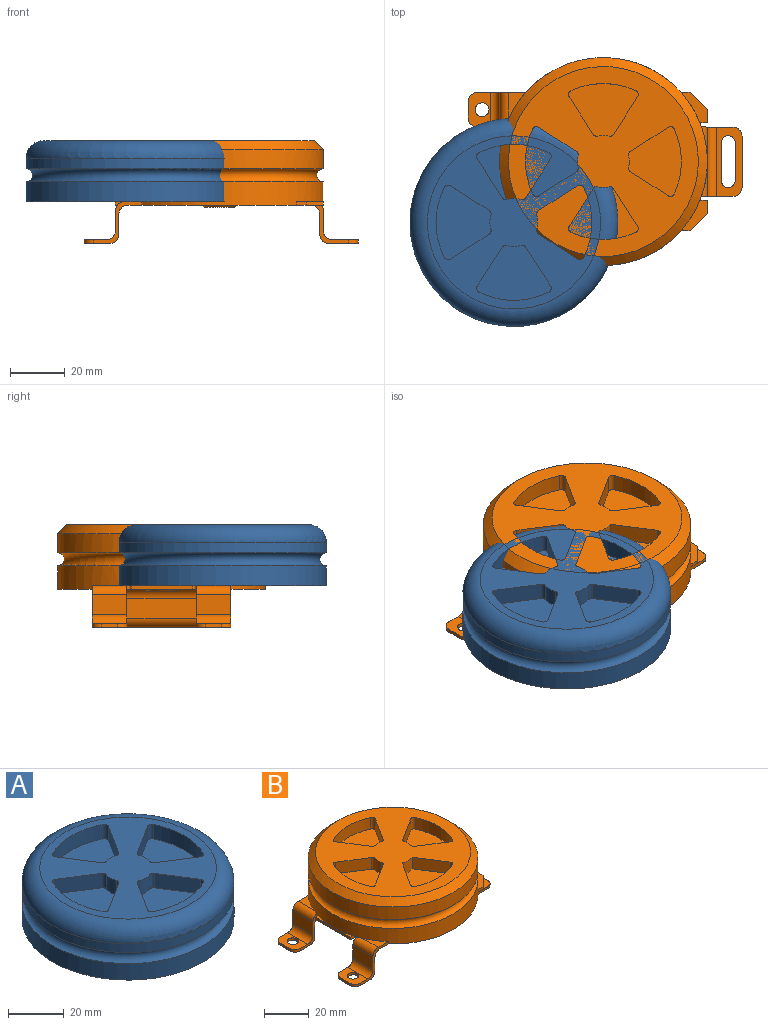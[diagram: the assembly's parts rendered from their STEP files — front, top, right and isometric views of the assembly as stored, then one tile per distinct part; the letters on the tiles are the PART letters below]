
ASSEMBLY  parts=2 mates=1
PART A: 48 faces, bbox 86.2x86.2x22.4 mm
  f0: cylinder r=38.1mm len=76.2mm, axis (0,0,-1), area 942.5mm2, adj f38,f41
  f1: plane 63.5x63.5mm, normal (0,0,1), area 1688.4mm2, adj f2,f3,f4,f5,f7,f8,f9,f10
  f2: cylinder r=28.57mm len=25.69mm, axis (0,0,1), area 169.2mm2, adj f1,f6,f34,f37
  f3: plane 14.28x9.1mm, normal (0.54,-0.84,0), area 107.5mm2, adj f1,f6,f36,f37
  f4: cylinder r=8.82mm len=6.35mm, axis (0,0,1), area 33.7mm2, adj f1,f6,f35,f36
  f5: plane 14.28x9.1mm, normal (0.54,0.84,0), area 107.5mm2, adj f1,f6,f34,f35
  f6: plane 27.37x20.21mm, normal (0,0,1), area 369.6mm2, adj f2,f3,f4,f5,f34,f35,f36,f37
  f7: cylinder r=8.82mm len=6.35mm, axis (0,0,1), area 33.7mm2, adj f1,f11,f22,f25
  f8: plane 14.28x9.1mm, normal (0.84,-0.54,0), area 107.5mm2, adj f1,f11,f24,f25
  f9: cylinder r=28.57mm len=25.69mm, axis (0,0,1), area 169.2mm2, adj f1,f11,f23,f24
  f10: plane 14.28x9.1mm, normal (-0.84,-0.54,0), area 107.5mm2, adj f1,f11,f22,f23
  f11: plane 27.37x20.21mm, normal (0,0,1), area 369.6mm2, adj f7,f8,f9,f10,f22,f23,f24,f25
  f12: cylinder r=8.82mm len=6.35mm, axis (0,0,1), area 33.7mm2, adj f1,f16,f30,f33
  f13: plane 14.28x9.1mm, normal (-0.84,0.54,0), area 107.5mm2, adj f1,f16,f30,f31
  f14: cylinder r=28.57mm len=25.69mm, axis (0,0,1), area 169.2mm2, adj f1,f16,f31,f32
  f15: plane 14.28x9.1mm, normal (0.84,0.54,0), area 107.5mm2, adj f1,f16,f32,f33
  f16: plane 27.37x20.21mm, normal (0,0,1), area 369.6mm2, adj f12,f13,f14,f15,f30,f31,f32,f33
  f17: cylinder r=8.82mm len=6.35mm, axis (0,0,1), area 33.7mm2, adj f1,f21,f26,f29
  f18: plane 14.28x9.1mm, normal (-0.54,-0.84,0), area 107.5mm2, adj f1,f21,f28,f29
  f19: cylinder r=28.57mm len=25.69mm, axis (0,0,1), area 169.2mm2, adj f1,f21,f27,f28
  f20: plane 14.28x9.1mm, normal (-0.54,0.84,0), area 107.5mm2, adj f1,f21,f26,f27
  f21: plane 27.37x20.21mm, normal (0,0,1), area 369.6mm2, adj f17,f18,f19,f20,f26,f27,f28,f29
  f22: cylinder r=1.52mm len=6.35mm, axis (0,0,1), area 12.6mm2, adj f1,f7,f10,f11
  f23: cylinder r=1.52mm len=6.35mm, axis (0,0,1), area 16.2mm2, adj f1,f9,f10,f11
  f24: cylinder r=1.52mm len=6.35mm, axis (0,0,1), area 16.2mm2, adj f1,f8,f9,f11
  f25: cylinder r=1.52mm len=6.35mm, axis (0,0,1), area 12.6mm2, adj f1,f7,f8,f11
  f26: cylinder r=1.52mm len=6.35mm, axis (0,0,1), area 12.6mm2, adj f1,f17,f20,f21
  f27: cylinder r=1.52mm len=6.35mm, axis (0,0,1), area 16.2mm2, adj f1,f19,f20,f21
  f28: cylinder r=1.52mm len=6.35mm, axis (0,0,1), area 16.2mm2, adj f1,f18,f19,f21
  f29: cylinder r=1.52mm len=6.35mm, axis (0,0,1), area 12.6mm2, adj f1,f17,f18,f21
  f30: cylinder r=1.52mm len=6.35mm, axis (0,0,1), area 12.6mm2, adj f1,f12,f13,f16
  f31: cylinder r=1.52mm len=6.35mm, axis (0,0,1), area 16.2mm2, adj f1,f13,f14,f16
  f32: cylinder r=1.52mm len=6.35mm, axis (0,0,1), area 16.2mm2, adj f1,f14,f15,f16
  f33: cylinder r=1.52mm len=6.35mm, axis (0,0,1), area 12.6mm2, adj f1,f12,f15,f16
  f34: cylinder r=1.52mm len=6.35mm, axis (0,0,1), area 16.2mm2, adj f1,f2,f5,f6
  f35: cylinder r=1.52mm len=6.35mm, axis (0,0,1), area 12.6mm2, adj f1,f4,f5,f6
  f36: cylinder r=1.52mm len=6.35mm, axis (0,0,1), area 12.6mm2, adj f1,f3,f4,f6
  f37: cylinder r=1.52mm len=6.35mm, axis (0,0,1), area 16.2mm2, adj f1,f2,f3,f6
  f38: torus R=38.1mm, axis (0,0,1), area 1741.6mm2, adj f0,f40
  f39: plane 76.2x76.2mm, normal (0,0,-1), area 4465.4mm2, adj f40,f42,f44,f46
  f40: cylinder r=38.1mm len=76.2mm, axis (0,0,-1), area 1732.9mm2, adj f38,f39
  f41: torus R=31.75mm, axis (0,0,1), area 2243.2mm2, adj f0,f1
  f42: cylinder r=3.17mm len=15.24mm, axis (0,0,-1), area 304mm2, adj f39,f43
  f43: plane 6.35x6.35mm, normal (0,0,-1), area 31.7mm2, adj f42
  f44: cylinder r=3.17mm len=15.24mm, axis (0,0,-1), area 304mm2, adj f39,f45
  f45: plane 6.35x6.35mm, normal (0,0,-1), area 31.7mm2, adj f44
  f46: cylinder r=3.17mm len=15.24mm, axis (0,0,-1), area 304mm2, adj f39,f47
  f47: plane 6.35x6.35mm, normal (0,0,-1), area 31.7mm2, adj f46
PART B: 111 faces, bbox 100.3x86.2x37.6 mm
  f0: plane 69.6x69.6mm, normal (0,0,1), area 2498.2mm2, adj f74,f75,f76,f77,f79,f80,f81,f82
  f1: cylinder r=38.1mm len=76.2mm, axis (0,0,-1), area 1895.7mm2, adj f2,f3,f4,f5,f6,f9,f10,f13
  f2: plane 11.18x9.7mm, normal (0,0,1), area 44.4mm2, adj f1,f17,f18,f47,f53
  f3: plane 9.89x6.4mm, normal (0,0,1), area 28mm2, adj f1,f16,f27
  f4: plane 11.18x1.68mm, normal (0,0,1), area 6.2mm2, adj f1,f11,f24
  f5: plane 11.18x1.68mm, normal (0,0,1), area 6.2mm2, adj f1,f11,f23
  f6: plane 9.89x6.4mm, normal (0,0,1), area 28mm2, adj f1,f14,f28
  f7: plane 25.4x7.37mm, normal (1,0,0), area 187.1mm2, adj f49,f50,f66,f68
  f8: plane 4.83x1.27mm, normal (1,0,0), area 6.1mm2, adj f9,f10,f48,f52
  f9: plane 11.18x9.7mm, normal (0,0,1), area 44.4mm2, adj f1,f8,f13,f48,f52
  f10: plane 76.2x76.2mm, normal (0,0,-1), area 4443.5mm2, adj f1,f8,f11,f13,f14,f16,f17,f18
  f11: plane 22.35x1.27mm, normal (-1,0,0), area 28.4mm2, adj f4,f5,f10,f23,f24
  f12: plane 12.7x7.37mm, normal (-1,0,0), area 93.5mm2, adj f14,f21,f28,f45
  f13: plane 3.35x1.27mm, normal (0,1,0), area 4.3mm2, adj f1,f9,f10,f48
  f14: plane 17.83x15.24mm, normal (0,1,0), area 40.4mm2, adj f1,f6,f10,f12,f22,f28,f29,f37
  f15: plane 12.7x7.37mm, normal (-1,0,0), area 93.5mm2, adj f16,f20,f27,f46
  f16: plane 17.83x15.24mm, normal (0,-1,0), area 40.4mm2, adj f1,f3,f10,f15,f19,f27,f30,f33
  f17: plane 3.35x1.27mm, normal (0,-1,0), area 4.3mm2, adj f1,f2,f10,f47
  f18: plane 4.83x1.27mm, normal (1,0,0), area 6.1mm2, adj f2,f10,f47,f53
  f19: plane 12.7x7.37mm, normal (1,0,0), area 93.5mm2, adj f16,f20,f30,f44
  f20: plane 15.24x11.94mm, normal (0,1,0), area 32.9mm2, adj f15,f19,f26,f27,f30,f33,f34,f43
  f21: plane 15.24x11.94mm, normal (0,-1,0), area 32.9mm2, adj f12,f22,f25,f28,f29,f37,f38,f40
  f22: plane 12.7x7.37mm, normal (1,0,0), area 93.5mm2, adj f14,f21,f29,f41
  f23: plane 3.81x1.27mm, normal (0,1,0), area 4.8mm2, adj f5,f10,f11,f25,f70
  f24: plane 3.81x1.27mm, normal (0,-1,0), area 4.8mm2, adj f4,f10,f11,f26,f71
  f25: cylinder r=0.76mm len=1.52mm, axis (0,0,-1), area 3.1mm2, adj f10,f21,f23,f29,f70
  f26: cylinder r=0.76mm len=1.52mm, axis (0,0,-1), area 3.1mm2, adj f10,f20,f24,f30,f71
  f27: cylinder r=3.3mm len=12.7mm, axis (0,1,0), area 65.9mm2, adj f3,f15,f16,f20,f71
  f28: cylinder r=3.3mm len=12.7mm, axis (0,1,0), area 65.9mm2, adj f6,f12,f14,f21,f70
  f29: cylinder r=3.3mm len=13.46mm, axis (0,1,0), area 66mm2, adj f10,f14,f21,f22,f25
  f30: cylinder r=3.3mm len=13.46mm, axis (0,1,0), area 66mm2, adj f10,f16,f19,f20,f26
  f31: plane 6.1x1.27mm, normal (-1,0,0), area 7.7mm2, adj f33,f34,f42,f43
  f32: cylinder r=2.54mm len=5.08mm, axis (0,0,1), area 20.3mm2, adj f33,f34
  f33: plane 12.7x9.4mm, normal (0,0,-1), area 94.4mm2, adj f16,f20,f31,f32,f42,f43,f44
  f34: plane 12.7x8.13mm, normal (0,0,1), area 78.3mm2, adj f16,f20,f31,f32,f42,f43,f46
  f35: plane 6.1x1.27mm, normal (-1,0,0), area 7.7mm2, adj f37,f38,f39,f40
  f36: cylinder r=2.54mm len=5.08mm, axis (0,0,1), area 20.3mm2, adj f37,f38
  f37: plane 12.7x9.4mm, normal (0,0,-1), area 94.4mm2, adj f14,f21,f35,f36,f39,f40,f41
  f38: plane 12.7x8.13mm, normal (0,0,1), area 78.3mm2, adj f14,f21,f35,f36,f39,f40,f45
  f39: cylinder r=3.3mm len=3.3mm, axis (0,0,-1), area 6.6mm2, adj f14,f35,f37,f38
  f40: cylinder r=3.3mm len=3.3mm, axis (0,0,1), area 6.6mm2, adj f21,f35,f37,f38
  f41: cylinder r=3.3mm len=12.7mm, axis (0,1,0), area 65.9mm2, adj f14,f21,f22,f37
  f42: cylinder r=3.3mm len=3.3mm, axis (0,0,1), area 6.6mm2, adj f16,f31,f33,f34
  f43: cylinder r=3.3mm len=3.3mm, axis (0,0,1), area 6.6mm2, adj f20,f31,f33,f34
  f44: cylinder r=3.3mm len=12.7mm, axis (0,1,0), area 65.9mm2, adj f16,f19,f20,f33
  f45: cylinder r=3.3mm len=12.7mm, axis (0,1,0), area 65.9mm2, adj f12,f14,f21,f38
  f46: cylinder r=3.3mm len=12.7mm, axis (0,1,0), area 65.9mm2, adj f15,f16,f20,f34
  f47: plane 6.35x6.35mm, normal (0.71,-0.71,0), area 11.4mm2, adj f2,f10,f17,f18
  f48: plane 6.35x6.35mm, normal (0.71,0.71,0), area 11.4mm2, adj f8,f9,f10,f13
  f49: plane 15.24x13.21mm, normal (0,1,0), area 34.5mm2, adj f7,f51,f54,f56,f62,f63,f65,f66
  f50: plane 15.24x13.21mm, normal (0,-1,0), area 34.5mm2, adj f7,f51,f55,f56,f62,f64,f65,f66
  f51: plane 25.4x7.37mm, normal (-1,0,0), area 187.1mm2, adj f49,f50,f65,f67
  f52: plane 3.81x1.27mm, normal (0,-1,0), area 4.8mm2, adj f8,f9,f10,f54,f69
  f53: plane 3.81x1.27mm, normal (0,1,0), area 4.8mm2, adj f2,f10,f18,f55,f69
  f54: cylinder r=0.76mm len=1.52mm, axis (0,0,-1), area 3.1mm2, adj f10,f49,f52,f67,f69
  f55: cylinder r=0.76mm len=1.52mm, axis (0,0,-1), area 3.1mm2, adj f10,f50,f53,f67,f69
  f56: plane 25.4x9.4mm, normal (0,0,1), area 142.8mm2, adj f49,f50,f57,f58,f59,f60,f61,f63
  f57: plane 13.97x1.27mm, normal (-1,0,0), area 17.7mm2, adj f56,f58,f61,f62
  f58: cylinder r=2.54mm len=5.08mm, axis (0,0,1), area 10.1mm2, adj f56,f57,f59,f62
  f59: plane 13.97x1.27mm, normal (1,0,0), area 17.7mm2, adj f56,f58,f61,f62
  f60: plane 18.8x1.27mm, normal (1,0,0), area 23.9mm2, adj f56,f62,f63,f64
  f61: cylinder r=2.54mm len=5.08mm, axis (0,0,1), area 10.1mm2, adj f56,f57,f59,f62
  f62: plane 25.4x10.67mm, normal (0,0,-1), area 175.1mm2, adj f49,f50,f57,f58,f59,f60,f61,f63
  f63: cylinder r=3.3mm len=3.3mm, axis (0,0,1), area 6.6mm2, adj f49,f56,f60,f62
  f64: cylinder r=3.3mm len=3.3mm, axis (0,0,-1), area 6.6mm2, adj f50,f56,f60,f62
  f65: cylinder r=3.3mm len=25.4mm, axis (0,-1,0), area 131.7mm2, adj f49,f50,f51,f62
  f66: cylinder r=3.3mm len=25.4mm, axis (0,-1,0), area 131.7mm2, adj f7,f49,f50,f69
  f67: cylinder r=3.3mm len=26.92mm, axis (0,-1,0), area 132mm2, adj f10,f49,f50,f51,f54,f55
  f68: cylinder r=3.3mm len=25.4mm, axis (0,-1,0), area 131.7mm2, adj f7,f49,f50,f56
  f69: plane 28.45x4.57mm, normal (0,0,-1), area 71.6mm2, adj f1,f49,f50,f52,f53,f54,f55,f66
  f70: plane 4.34x2.9mm, normal (0,0,-1), area 5.4mm2, adj f1,f21,f23,f25,f28
  f71: plane 4.34x2.9mm, normal (0,0,-1), area 5.4mm2, adj f1,f20,f24,f26,f27
  f72: torus R=38.1mm, axis (0,0,1), area 1741.6mm2, adj f1,f73
  f73: cylinder r=38.1mm len=76.2mm, axis (0,0,-1), area 1672.1mm2, adj f72,f108
  f74: cylinder r=9.53mm len=6.35mm, axis (0,0,1), area 40.6mm2, adj f0,f75,f77,f78
  f75: plane 14.78x9.42mm, normal (0.84,-0.54,0), area 111.3mm2, adj f0,f74,f78,f107
  f76: cylinder r=28.57mm len=23.81mm, axis (0,0,1), area 155.9mm2, adj f0,f78,f106,f107
  f77: plane 14.78x9.42mm, normal (-0.84,-0.54,0), area 111.3mm2, adj f0,f74,f78,f106
  f78: plane 25.58x19.58mm, normal (0,0,1), area 326.8mm2, adj f74,f75,f76,f77,f106,f107
  f79: cylinder r=9.53mm len=6.35mm, axis (0,0,1), area 27.2mm2, adj f0,f83,f95,f96
  f80: plane 13.82x8.81mm, normal (-0.54,-0.84,0), area 104.1mm2, adj f0,f83,f94,f95
  f81: cylinder r=28.57mm len=23.81mm, axis (0,0,1), area 155.9mm2, adj f0,f83,f94,f97
  f82: plane 13.82x8.81mm, normal (-0.54,0.84,0), area 104.1mm2, adj f0,f83,f96,f97
  f83: plane 25.58x19.33mm, normal (0,0,1), area 326.4mm2, adj f79,f80,f81,f82,f94,f95,f96,f97
  f84: cylinder r=9.53mm len=6.35mm, axis (0,0,1), area 27.2mm2, adj f0,f88,f102,f105
  f85: plane 13.82x8.81mm, normal (0.54,0.84,0), area 104.1mm2, adj f0,f88,f102,f103
  f86: cylinder r=28.57mm len=23.81mm, axis (0,0,1), area 155.9mm2, adj f0,f88,f103,f104
  f87: plane 13.82x8.81mm, normal (0.54,-0.84,0), area 104.1mm2, adj f0,f88,f104,f105
  f88: plane 25.58x19.33mm, normal (0,0,1), area 326.4mm2, adj f84,f85,f86,f87,f102,f103,f104,f105
  f89: cylinder r=9.53mm len=6.35mm, axis (0,0,1), area 27.2mm2, adj f0,f93,f98,f101
  f90: plane 13.82x8.81mm, normal (-0.84,0.54,0), area 104.1mm2, adj f0,f93,f100,f101
  f91: cylinder r=28.57mm len=23.81mm, axis (0,0,1), area 155.9mm2, adj f0,f93,f99,f100
  f92: plane 13.82x8.81mm, normal (0.84,0.54,0), area 104.1mm2, adj f0,f93,f98,f99
  f93: plane 25.58x19.33mm, normal (0,0,1), area 326.4mm2, adj f89,f90,f91,f92,f98,f99,f100,f101
  f94: cylinder r=1.52mm len=6.35mm, axis (0,0,1), area 16.5mm2, adj f0,f80,f81,f83
  f95: cylinder r=1.52mm len=6.35mm, axis (0,0,1), area 11.9mm2, adj f0,f79,f80,f83
  f96: cylinder r=1.52mm len=6.35mm, axis (0,0,1), area 11.9mm2, adj f0,f79,f82,f83
  f97: cylinder r=1.52mm len=6.35mm, axis (0,0,1), area 16.5mm2, adj f0,f81,f82,f83
  f98: cylinder r=1.52mm len=6.35mm, axis (0,0,1), area 11.9mm2, adj f0,f89,f92,f93
  f99: cylinder r=1.52mm len=6.35mm, axis (0,0,1), area 16.5mm2, adj f0,f91,f92,f93
  f100: cylinder r=1.52mm len=6.35mm, axis (0,0,1), area 16.5mm2, adj f0,f90,f91,f93
  f101: cylinder r=1.52mm len=6.35mm, axis (0,0,1), area 11.9mm2, adj f0,f89,f90,f93
  f102: cylinder r=1.52mm len=6.35mm, axis (0,0,1), area 11.9mm2, adj f0,f84,f85,f88
  f103: cylinder r=1.52mm len=6.35mm, axis (0,0,1), area 16.5mm2, adj f0,f85,f86,f88
  f104: cylinder r=1.52mm len=6.35mm, axis (0,0,1), area 16.5mm2, adj f0,f86,f87,f88
  f105: cylinder r=1.52mm len=6.35mm, axis (0,0,1), area 11.9mm2, adj f0,f84,f87,f88
  f106: cylinder r=1.52mm len=6.35mm, axis (0,0,1), area 16.5mm2, adj f0,f76,f77,f78
  f107: cylinder r=1.52mm len=6.35mm, axis (0,0,1), area 16.5mm2, adj f0,f75,f76,f78
  f108: cone r=34.8mm half-angle=45deg, axis (0,0,-1), area 1069.4mm2, adj f0,f73
  f109: plane 11.18x11.18mm, normal (0,0,-1), area 98.1mm2, adj f110
  f110: cone r=6.35mm half-angle=45deg, axis (0,0,1), area 40.4mm2, adj f10,f109
PLACE A t=(-31.38,-24.72,24.87)mm
PLACE B t=(1.4,-2.41,23.6)mm
MATE fastened B.f3 <-> A.f0  axis (0,0,1) through (-31.38,-24.72,24.87)mm
